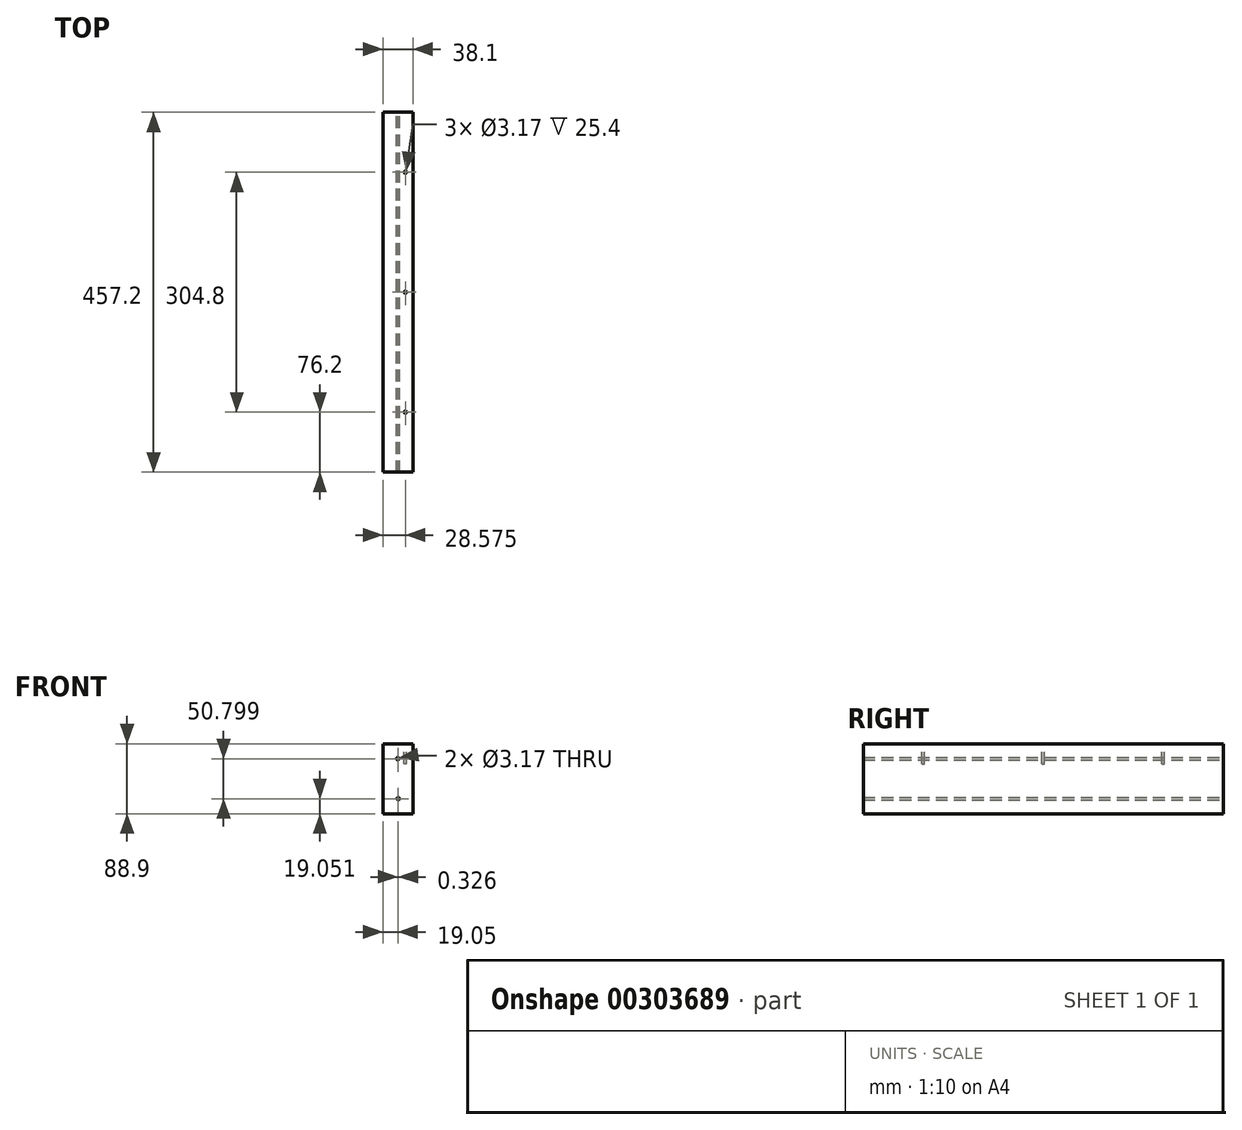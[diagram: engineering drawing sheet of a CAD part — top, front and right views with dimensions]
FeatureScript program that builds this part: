
annotation { "Feature Type Name" : "Feature", "Feature Type Description" : "" }
export const myFeature = defineFeature(function(context is Context, id is Id, definition is map)
    precondition{}
    {
        {
            var Q0;
            Q0=qCreatedBy(makeId("Front.planeOp"),FACE);
            var sketch = newSketch(context, id + "F0", { "sketchPlane" : qUnion([Q0])});
            skLineSegment(sketch, "E0.bottom", {"start": v(0, 0) * mm, "end": v(38.1, 0) * mm});
            skLineSegment(sketch, "E0.top", {"start": v(0, -88.9) * mm, "end": v(38.1, -88.9) * mm});
            skLineSegment(sketch, "E0.left", {"start": v(0, 0) * mm, "end": v(0, -88.9) * mm});
            skLineSegment(sketch, "E0.right", {"start": v(38.1, 0) * mm, "end": v(38.1, -88.9) * mm});
            skSolve(sketch);
        }
        {
            var Q0;
            Q0=qSketchRegion(id+"F0",true);
            extrude(context, id + "F1", {"entities" : qUnion([Q0]), "depth" : 457.2 * mm});
        }
        {
            var Q0;
            Q0=qCreatedBy(makeId("Front.planeOp"),FACE);
            var sketch = newSketch(context, id + "F2", { "sketchPlane" : qUnion([Q0])});
            skCircle(sketch, "E1", {"center": v(19.05, -19.05) * mm, "radius": 1.59 * mm});
            skCircle(sketch, "E2.1.0.0", {"center": v(19.38, -69.85) * mm, "radius": 1.59 * mm});
            skLineSegment(sketch, "E2.direction1", {"start": v(19.05, -19.05) * mm, "end": v(19.38, -69.85) * mm, "construction": true});
            skSolve(sketch);
        }
        {
            var Q0;
            Q0=qSketchRegion(id+"F2",true);
            extrude(context, id + "F3", {"entities" : qUnion([Q0]), "operationType" : NewBodyOperationType.REMOVE, "depth" : 457.2 * mm});
        }
        {
            var Q0;
            Q0=qCreatedBy(makeId("Top.planeOp"),FACE);
            var sketch = newSketch(context, id + "F4", { "sketchPlane" : qUnion([Q0])});
            skCircle(sketch, "E3", {"center": v(28.57, -76.2) * mm, "radius": 1.59 * mm});
            skCircle(sketch, "E4.1.0.0", {"center": v(28.57, -228.6) * mm, "radius": 1.59 * mm});
            skCircle(sketch, "E4.2.0.0", {"center": v(28.57, -381) * mm, "radius": 1.59 * mm});
            skLineSegment(sketch, "E4.direction1", {"start": v(28.57, -76.2) * mm, "end": v(28.57, -228.6) * mm, "construction": true});
            skSolve(sketch);
        }
        {
            var Q0;
            Q0=qSketchRegion(id+"F4",true);
            extrude(context, id + "F5", {"entities" : qUnion([Q0]), "operationType" : NewBodyOperationType.REMOVE, "oppositeDirection" : true, "depth" : 25.4 * mm});
        }
    });
